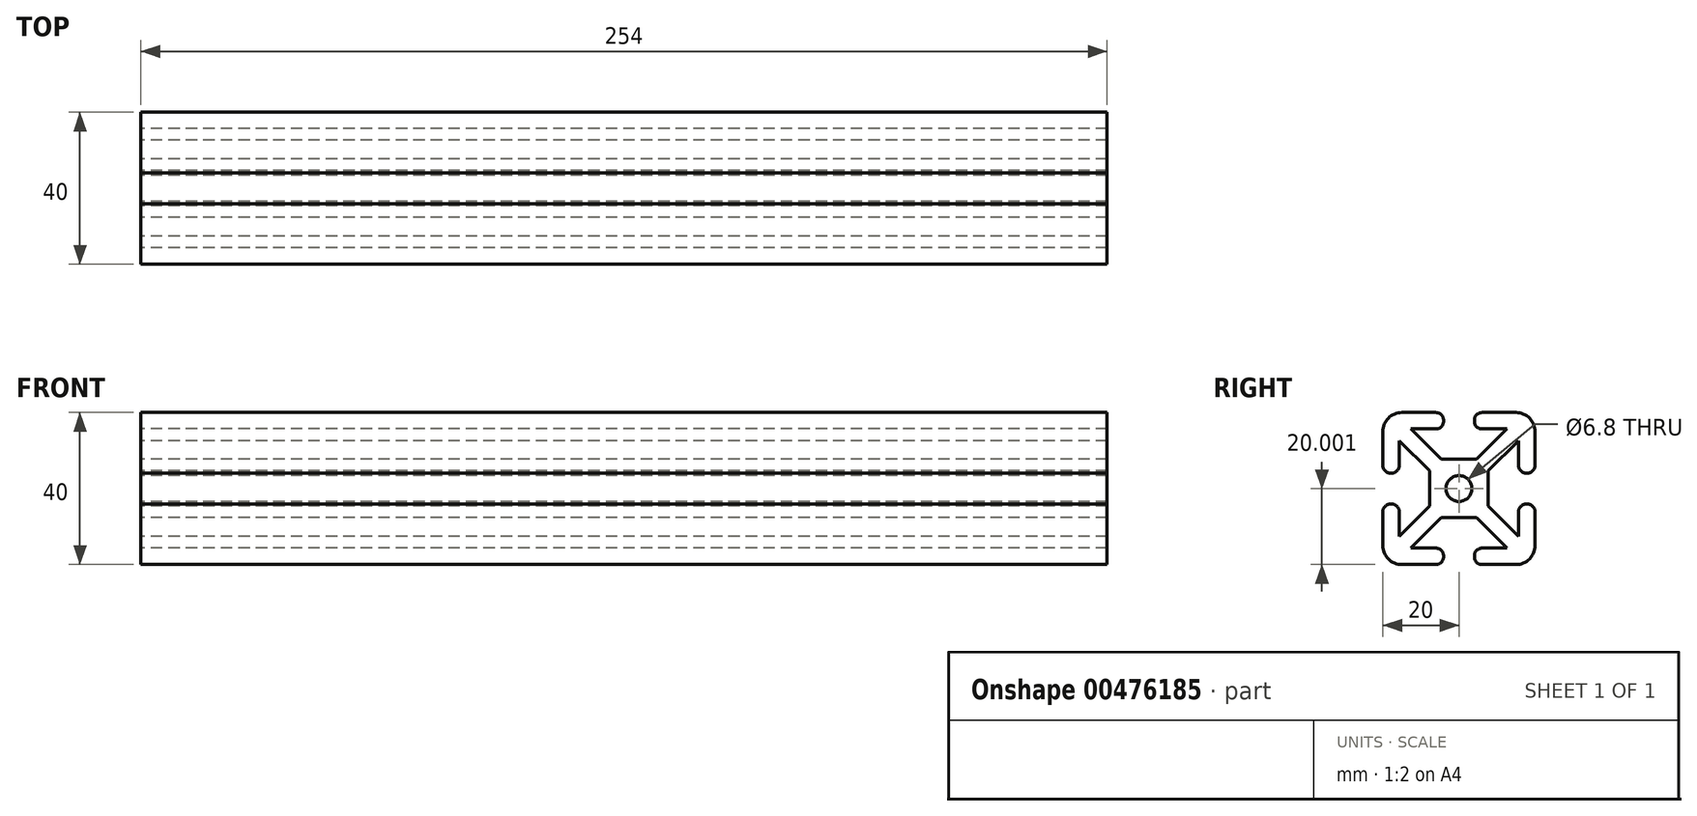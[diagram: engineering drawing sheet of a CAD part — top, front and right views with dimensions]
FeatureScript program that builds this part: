
annotation { "Feature Type Name" : "Feature", "Feature Type Description" : "" }
export const myFeature = defineFeature(function(context is Context, id is Id, definition is map)
    precondition{}
    {
        {
            var Q0;
            Q0=qCreatedBy(makeId("Right.planeOp"),FACE);
            var sketch = newSketch(context, id + "F0", { "sketchPlane" : qUnion([Q0])});
            skLineSegment(sketch, "E0", {"start": v(-15.94, 15.35) * mm, "end": v(0, 15.35) * mm});
            skLineSegment(sketch, "E1", {"start": v(0, 15.35) * mm, "end": v(8.12, 15.35) * mm, "construction": true});
            skLineSegment(sketch, "E2", {"start": v(8.12, 15.35) * mm, "end": v(24.06, 15.35) * mm});
            skLineSegment(sketch, "E3.bottom", {"start": v(-3.62, 3.04) * mm, "end": v(11.75, 3.04) * mm});
            skLineSegment(sketch, "E3.top", {"start": v(-3.62, -12.33) * mm, "end": v(11.75, -12.33) * mm});
            skLineSegment(sketch, "E3.left", {"start": v(-3.62, 3.04) * mm, "end": v(-3.62, -12.33) * mm});
            skLineSegment(sketch, "E3.right", {"start": v(11.75, 3.04) * mm, "end": v(11.75, -12.33) * mm});
            skLineSegment(sketch, "E4", {"start": v(11.74, 3.04) * mm, "end": v(24.06, 15.35) * mm, "construction": true});
            skLineSegment(sketch, "E5", {"start": v(-3.62, 3.04) * mm, "end": v(-15.94, 15.35) * mm});
            skLineSegment(sketch, "E6", {"start": v(-3.62, -12.33) * mm, "end": v(-15.94, -24.65) * mm, "construction": true});
            skLineSegment(sketch, "E7", {"start": v(11.74, -12.33) * mm, "end": v(24.06, -24.65) * mm});
            skLineSegment(sketch, "E8", {"start": v(16.5, 7.78) * mm, "end": v(14.97, 9.31) * mm, "construction": true});
            skLineSegment(sketch, "E9", {"start": v(16.5, 7.78) * mm, "end": v(18.02, 6.26) * mm, "construction": true});
            skLineSegment(sketch, "E10", {"start": v(14.97, 9.31) * mm, "end": v(21, 15.35) * mm});
            skLineSegment(sketch, "E11", {"start": v(18.02, 6.26) * mm, "end": v(24.06, 12.3) * mm});
            skLineSegment(sketch, "E12", {"start": v(14.97, 9.31) * mm, "end": v(-15.94, -21.6) * mm});
            skLineSegment(sketch, "E13", {"start": v(18.02, 6.26) * mm, "end": v(-12.89, -24.65) * mm});
            skLineSegment(sketch, "E14", {"start": v(0, 15.35) * mm, "end": v(0, 11.03) * mm});
            skLineSegment(sketch, "E15", {"start": v(8.12, 15.35) * mm, "end": v(8.12, 11.03) * mm});
            skLineSegment(sketch, "E16", {"start": v(8.12, 11.03) * mm, "end": v(16.69, 11.03) * mm});
            skLineSegment(sketch, "E17", {"start": v(0, 11.03) * mm, "end": v(-11.62, 11.03) * mm});
            skLineSegment(sketch, "E18", {"start": v(-3.62, 3.04) * mm, "end": v(11.75, -12.33) * mm});
            skLineSegment(sketch, "E19", {"start": v(11.74, 3.04) * mm, "end": v(-3.62, -12.33) * mm, "construction": true});
            skCircle(sketch, "E20", {"center": v(4.06, -4.65) * mm, "radius": 3.4 * mm});
            skLineSegment(sketch, "E21", {"start": v(24.06, -0.59) * mm, "end": v(24.06, -8.7) * mm, "construction": true});
            skLineSegment(sketch, "E22", {"start": v(24.06, -0.59) * mm, "end": v(24.06, 15.35) * mm});
            skLineSegment(sketch, "E23", {"start": v(24.06, -24.65) * mm, "end": v(24.06, -8.7) * mm});
            skLineSegment(sketch, "E24", {"start": v(24.06, -0.59) * mm, "end": v(19.74, -0.59) * mm});
            skLineSegment(sketch, "E25", {"start": v(24.06, -8.7) * mm, "end": v(19.74, -8.7) * mm});
            skLineSegment(sketch, "E26", {"start": v(19.74, -0.59) * mm, "end": v(19.74, 7.98) * mm});
            skLineSegment(sketch, "E27", {"start": v(19.74, 7.98) * mm, "end": v(16.69, 11.03) * mm});
            skLineSegment(sketch, "E28", {"start": v(-7.27, 6.68) * mm, "end": v(-8.8, 5.15) * mm});
            skLineSegment(sketch, "E29", {"start": v(-7.27, 6.68) * mm, "end": v(-5.74, 8.2) * mm});
            skLineSegment(sketch, "E30", {"start": v(-5.74, 8.2) * mm, "end": v(-12.89, 15.35) * mm});
            skLineSegment(sketch, "E31", {"start": v(-5.74, 8.2) * mm, "end": v(24.06, -21.6) * mm});
            skLineSegment(sketch, "E32", {"start": v(19.74, -8.7) * mm, "end": v(19.74, -17.27) * mm});
            skLineSegment(sketch, "E33", {"start": v(-15.94, 15.35) * mm, "end": v(-15.94, -0.59) * mm});
            skLineSegment(sketch, "E34", {"start": v(-15.94, -0.59) * mm, "end": v(-15.94, -8.7) * mm, "construction": true});
            skLineSegment(sketch, "E35", {"start": v(-15.94, -24.65) * mm, "end": v(0, -24.65) * mm});
            skLineSegment(sketch, "E36", {"start": v(0, -24.65) * mm, "end": v(8.12, -24.65) * mm, "construction": true});
            skLineSegment(sketch, "E37", {"start": v(-15.94, -8.7) * mm, "end": v(-15.94, -24.65) * mm});
            skLineSegment(sketch, "E38", {"start": v(8.12, -24.65) * mm, "end": v(24.06, -24.65) * mm});
            skLineSegment(sketch, "E39", {"start": v(-8.8, 5.15) * mm, "end": v(-15.94, 12.3) * mm});
            skLineSegment(sketch, "E40", {"start": v(-8.8, 5.15) * mm, "end": v(21, -24.65) * mm});
            skLineSegment(sketch, "E41", {"start": v(-15.94, -0.59) * mm, "end": v(-11.62, -0.59) * mm});
            skLineSegment(sketch, "E42", {"start": v(-15.94, -8.7) * mm, "end": v(-11.62, -8.7) * mm});
            skLineSegment(sketch, "E43", {"start": v(0, -24.65) * mm, "end": v(0, -20.33) * mm});
            skLineSegment(sketch, "E44", {"start": v(8.12, -24.65) * mm, "end": v(8.12, -20.33) * mm});
            skLineSegment(sketch, "E45", {"start": v(-11.62, -0.59) * mm, "end": v(-11.62, 7.98) * mm});
            skLineSegment(sketch, "E46", {"start": v(-11.62, -8.7) * mm, "end": v(-11.62, -17.27) * mm});
            skLineSegment(sketch, "E47", {"start": v(0, -20.33) * mm, "end": v(-8.57, -20.33) * mm});
            skLineSegment(sketch, "E48", {"start": v(8.12, -20.33) * mm, "end": v(16.69, -20.33) * mm});
            skSolve(sketch);
        }
        {
            var Q0;
            {var subQ0=sQuery(id+"F0.wireOp",EDGE,"E41");Q0=makeQuery(id+"F0.imprint","IMPRINT",FACE,{"disambiguationData":[TD([[makeQuery(id+"F0.imprint","IMPRINT",EDGE,{"derivedFrom":subQ0}),1.0]])]});}
            var Q1;
            {var subQ0=sQuery(id+"F0.wireOp",EDGE,"E28");Q1=makeQuery(id+"F0.imprint","IMPRINT",FACE,{"disambiguationData":[TD([[makeQuery(id+"F0.imprint","IMPRINT",EDGE,{"derivedFrom":subQ0}),-1.0]])]});}
            var Q2;
            {var subQ3=sQuery(id+"F0.wireOp",EDGE,"E29");Q2=makeQuery(id+"F0.imprint","IMPRINT",FACE,{"disambiguationData":[TD([[makeQuery(id+"F0.imprint","IMPRINT",EDGE,{"derivedFrom":subQ3}),1.0]])]});}
            var Q3;
            {var subQ0=sQuery(id+"F0.wireOp",EDGE,"E14");Q3=makeQuery(id+"F0.imprint","IMPRINT",FACE,{"disambiguationData":[TD([[makeQuery(id+"F0.imprint","IMPRINT",EDGE,{"derivedFrom":subQ0}),-1.0]])]});}
            var Q4;
            {var subQ0=sQuery(id+"F0.wireOp",EDGE,"E5");var subQ5=sQuery(id+"F0.wireOp",EDGE,"E17");var subQ6=makeQuery(id+"F0.imprint","INTERSECT",VERTEX,{"derivedFrom":[subQ0,subQ5]});Q4=makeQuery(id+"F0.imprint","IMPRINT",FACE,{"disambiguationData":[TD([[makeQuery(id+"F0.imprint","IMPRINT",EDGE,{"disambiguationData":[TD([[subQ6,1.0]])],"derivedFrom":subQ5}),-1.0]])]});}
            var Q5;
            {var subQ4=sQuery(id+"F0.wireOp",EDGE,"E42");Q5=makeQuery(id+"F0.imprint","IMPRINT",FACE,{"disambiguationData":[TD([[makeQuery(id+"F0.imprint","IMPRINT",EDGE,{"derivedFrom":subQ4}),-1.0]])]});}
            var Q6;
            {var subQ2=sQuery(id+"F0.wireOp",EDGE,"E3.left");var subQ6=sQuery(id+"F0.wireOp",EDGE,"E3.top");var subQ7=makeQuery(id+"F0.imprint","INTERSECT",VERTEX,{"derivedFrom":[subQ6,subQ2]});Q6=makeQuery(id+"F0.imprint","IMPRINT",FACE,{"disambiguationData":[TD([[makeQuery(id+"F0.imprint","IMPRINT",EDGE,{"disambiguationData":[TD([[subQ7,-1.0]])],"derivedFrom":subQ6}),-1.0]])]});}
            var Q7;
            {var subQ4=sQuery(id+"F0.wireOp",EDGE,"E43");Q7=makeQuery(id+"F0.imprint","IMPRINT",FACE,{"disambiguationData":[TD([[makeQuery(id+"F0.imprint","IMPRINT",EDGE,{"derivedFrom":subQ4}),1.0]])]});}
            var Q8;
            {var subQ3=sQuery(id+"F0.wireOp",EDGE,"E27");Q8=makeQuery(id+"F0.imprint","IMPRINT",FACE,{"disambiguationData":[TD([[makeQuery(id+"F0.imprint","IMPRINT",EDGE,{"derivedFrom":subQ3}),1.0]])]});}
            var Q9;
            {var subQ3=sQuery(id+"F0.wireOp",EDGE,"E27");Q9=makeQuery(id+"F0.imprint","IMPRINT",FACE,{"disambiguationData":[TD([[makeQuery(id+"F0.imprint","IMPRINT",EDGE,{"derivedFrom":subQ3}),-1.0]])]});}
            var Q10;
            {var subQ4=sQuery(id+"F0.wireOp",EDGE,"E24");Q10=makeQuery(id+"F0.imprint","IMPRINT",FACE,{"disambiguationData":[TD([[makeQuery(id+"F0.imprint","IMPRINT",EDGE,{"derivedFrom":subQ4}),-1.0]])]});}
            var Q11;
            {var subQ0=sQuery(id+"F0.wireOp",EDGE,"E15");Q11=makeQuery(id+"F0.imprint","IMPRINT",FACE,{"disambiguationData":[TD([[makeQuery(id+"F0.imprint","IMPRINT",EDGE,{"derivedFrom":subQ0}),1.0]])]});}
            var Q12;
            {var subQ0=sQuery(id+"F0.wireOp",EDGE,"E13");var subQ1=sQuery(id+"F0.wireOp",EDGE,"E3.right");var subQ2=makeQuery(id+"F0.imprint","INTERSECT",VERTEX,{"derivedFrom":[subQ1,subQ0]});Q12=makeQuery(id+"F0.imprint","IMPRINT",FACE,{"disambiguationData":[TD([[makeQuery(id+"F0.imprint","IMPRINT",EDGE,{"disambiguationData":[TD([[subQ2,-1.0]])],"derivedFrom":subQ1}),-1.0]])]});}
            var Q13;
            {var subQ0=sQuery(id+"F0.wireOp",EDGE,"E13");var subQ1=sQuery(id+"F0.wireOp",EDGE,"E3.top");var subQ2=makeQuery(id+"F0.imprint","INTERSECT",VERTEX,{"derivedFrom":[subQ1,subQ0]});Q13=makeQuery(id+"F0.imprint","IMPRINT",FACE,{"disambiguationData":[TD([[makeQuery(id+"F0.imprint","IMPRINT",EDGE,{"disambiguationData":[TD([[subQ2,-1.0]])],"derivedFrom":subQ1}),1.0]])]});}
            var Q14;
            {var subQ0=sQuery(id+"F0.wireOp",EDGE,"E40");var subQ1=sQuery(id+"F0.wireOp",EDGE,"E3.left");var subQ2=makeQuery(id+"F0.imprint","INTERSECT",VERTEX,{"derivedFrom":[subQ1,subQ0]});Q14=makeQuery(id+"F0.imprint","IMPRINT",FACE,{"disambiguationData":[TD([[makeQuery(id+"F0.imprint","IMPRINT",EDGE,{"disambiguationData":[TD([[subQ2,-1.0]])],"derivedFrom":subQ1}),1.0]])]});}
            var Q15;
            {var subQ0=sQuery(id+"F0.wireOp",EDGE,"E31");var subQ1=sQuery(id+"F0.wireOp",EDGE,"E3.bottom");var subQ2=makeQuery(id+"F0.imprint","INTERSECT",VERTEX,{"derivedFrom":[subQ1,subQ0]});Q15=makeQuery(id+"F0.imprint","IMPRINT",FACE,{"disambiguationData":[TD([[makeQuery(id+"F0.imprint","IMPRINT",EDGE,{"disambiguationData":[TD([[subQ2,-1.0]])],"derivedFrom":subQ1}),-1.0]])]});}
            var Q16;
            {var subQ5=sQuery(id+"F0.wireOp",EDGE,"E29");Q16=makeQuery(id+"F0.imprint","IMPRINT",FACE,{"disambiguationData":[TD([[makeQuery(id+"F0.imprint","IMPRINT",EDGE,{"derivedFrom":subQ5}),-1.0]])]});}
            var Q17;
            {var subQ5=sQuery(id+"F0.wireOp",EDGE,"E28");Q17=makeQuery(id+"F0.imprint","IMPRINT",FACE,{"disambiguationData":[TD([[makeQuery(id+"F0.imprint","IMPRINT",EDGE,{"derivedFrom":subQ5}),1.0]])]});}
            var Q18;
            {var subQ1=sQuery(id+"F0.wireOp",EDGE,"E7");Q18=makeQuery(id+"F0.imprint","IMPRINT",FACE,{"disambiguationData":[TD([[makeQuery(id+"F0.imprint","IMPRINT",EDGE,{"derivedFrom":subQ1}),-1.0]])]});}
            var Q19;
            {var subQ1=sQuery(id+"F0.wireOp",EDGE,"E7");Q19=makeQuery(id+"F0.imprint","IMPRINT",FACE,{"disambiguationData":[TD([[makeQuery(id+"F0.imprint","IMPRINT",EDGE,{"derivedFrom":subQ1}),1.0]])]});}
            var Q20;
            {var subQ0=sQuery(id+"F0.wireOp",EDGE,"E25");Q20=makeQuery(id+"F0.imprint","IMPRINT",FACE,{"disambiguationData":[TD([[makeQuery(id+"F0.imprint","IMPRINT",EDGE,{"derivedFrom":subQ0}),1.0]])]});}
            var Q21;
            {var subQ0=sQuery(id+"F0.wireOp",EDGE,"E44");Q21=makeQuery(id+"F0.imprint","IMPRINT",FACE,{"disambiguationData":[TD([[makeQuery(id+"F0.imprint","IMPRINT",EDGE,{"derivedFrom":subQ0}),-1.0]])]});}
            var Q22;
            {var subQ1=sQuery(id+"F0.wireOp",EDGE,"E3.right");var subQ6=sQuery(id+"F0.wireOp",EDGE,"E3.bottom");var subQ9=makeQuery(id+"F0.imprint","INTERSECT",VERTEX,{"derivedFrom":[subQ6,subQ1]});Q22=makeQuery(id+"F0.imprint","IMPRINT",FACE,{"disambiguationData":[TD([[makeQuery(id+"F0.imprint","IMPRINT",EDGE,{"disambiguationData":[TD([[subQ9,1.0]])],"derivedFrom":subQ6}),-1.0]])]});}
            var Q23;
            {var subQ0=sQuery(id+"F0.wireOp",EDGE,"E18");var subQ5=sQuery(id+"F0.wireOp",EDGE,"E20");var subQ6=makeQuery(id+"F0.imprint","INTERSECT",VERTEX,{"disambiguationData":[OD(0.0)],"derivedFrom":[subQ0,subQ5]});Q23=makeQuery(id+"F0.imprint","IMPRINT",FACE,{"disambiguationData":[TD([[makeQuery(id+"F0.imprint","IMPRINT",EDGE,{"disambiguationData":[TD([[subQ6,-1.0]])],"derivedFrom":subQ5}),-1.0]])]});}
            var Q24;
            {var subQ1=sQuery(id+"F0.wireOp",EDGE,"E3.top");var subQ6=sQuery(id+"F0.wireOp",EDGE,"E3.left");var subQ9=makeQuery(id+"F0.imprint","INTERSECT",VERTEX,{"derivedFrom":[subQ1,subQ6]});Q24=makeQuery(id+"F0.imprint","IMPRINT",FACE,{"disambiguationData":[TD([[makeQuery(id+"F0.imprint","IMPRINT",EDGE,{"disambiguationData":[TD([[subQ9,-1.0]])],"derivedFrom":subQ1}),1.0]])]});}
            var Q25;
            {var subQ0=sQuery(id+"F0.wireOp",EDGE,"E18");var subQ5=sQuery(id+"F0.wireOp",EDGE,"E20");var subQ6=makeQuery(id+"F0.imprint","INTERSECT",VERTEX,{"disambiguationData":[OD(1.0)],"derivedFrom":[subQ0,subQ5]});Q25=makeQuery(id+"F0.imprint","IMPRINT",FACE,{"disambiguationData":[TD([[makeQuery(id+"F0.imprint","IMPRINT",EDGE,{"disambiguationData":[TD([[subQ6,1.0]])],"derivedFrom":subQ5}),-1.0]])]});}
            var Q26;
            {var subQ0=sQuery(id+"F0.wireOp",EDGE,"E18");var subQ5=sQuery(id+"F0.wireOp",EDGE,"E20");var subQ6=makeQuery(id+"F0.imprint","INTERSECT",VERTEX,{"disambiguationData":[OD(1.0)],"derivedFrom":[subQ0,subQ5]});Q26=makeQuery(id+"F0.imprint","IMPRINT",FACE,{"disambiguationData":[TD([[makeQuery(id+"F0.imprint","IMPRINT",EDGE,{"disambiguationData":[TD([[subQ6,-1.0]])],"derivedFrom":subQ5}),-1.0]])]});}
            var Q27;
            {var subQ0=sQuery(id+"F0.wireOp",EDGE,"E18");var subQ5=sQuery(id+"F0.wireOp",EDGE,"E20");var subQ6=makeQuery(id+"F0.imprint","INTERSECT",VERTEX,{"disambiguationData":[OD(0.0)],"derivedFrom":[subQ0,subQ5]});Q27=makeQuery(id+"F0.imprint","IMPRINT",FACE,{"disambiguationData":[TD([[makeQuery(id+"F0.imprint","IMPRINT",EDGE,{"disambiguationData":[TD([[subQ6,1.0]])],"derivedFrom":subQ5}),-1.0]])]});}
            extrude(context, id + "F1", {"entities" : qUnion([Q0, Q1, Q2, Q3, Q4, Q5, Q6, Q7, Q8, Q9, Q10, Q11, Q12, Q13, Q14, Q15, Q16, Q17, Q18, Q19, Q20, Q21, Q22, Q23, Q24, Q25, Q26, Q27]), "depth" : 254 * mm});
        }
        {
            var Q0;
            Q0=makeQuery(id+"F1.opExtrude","SWEPT_EDGE",EDGE,{"disambiguationData":[OSD([sQuery(id+"F0.wireOp",EDGE,"E14"),sQuery(id+"F0.wireOp",EDGE,"E17")])]});
            var Q1;
            Q1=makeQuery(id+"F1.opExtrude","SWEPT_EDGE",EDGE,{"disambiguationData":[OSD([sQuery(id+"F0.wireOp",EDGE,"E41"),sQuery(id+"F0.wireOp",EDGE,"E45")])]});
            var Q2;
            Q2=makeQuery(id+"F1.opExtrude","SWEPT_EDGE",EDGE,{"disambiguationData":[OSD([sQuery(id+"F0.wireOp",EDGE,"E33"),sQuery(id+"F0.wireOp",EDGE,"E41")])]});
            var Q3;
            Q3=makeQuery(id+"F1.opExtrude","SWEPT_EDGE",EDGE,{"disambiguationData":[OSD([sQuery(id+"F0.wireOp",EDGE,"E0"),sQuery(id+"F0.wireOp",EDGE,"E14")])]});
            var Q4;
            Q4=makeQuery(id+"F1.opExtrude","SWEPT_EDGE",EDGE,{"disambiguationData":[OSD([sQuery(id+"F0.wireOp",EDGE,"E15"),sQuery(id+"F0.wireOp",EDGE,"E16")])]});
            var Q5;
            Q5=makeQuery(id+"F1.opExtrude","SWEPT_EDGE",EDGE,{"disambiguationData":[OSD([sQuery(id+"F0.wireOp",EDGE,"E24"),sQuery(id+"F0.wireOp",EDGE,"E26")])]});
            var Q6;
            Q6=makeQuery(id+"F1.opExtrude","SWEPT_EDGE",EDGE,{"disambiguationData":[OSD([sQuery(id+"F0.wireOp",EDGE,"E22"),sQuery(id+"F0.wireOp",EDGE,"E24")])]});
            var Q7;
            Q7=makeQuery(id+"F1.opExtrude","SWEPT_EDGE",EDGE,{"disambiguationData":[OSD([sQuery(id+"F0.wireOp",EDGE,"E38"),sQuery(id+"F0.wireOp",EDGE,"E44")])]});
            var Q8;
            Q8=makeQuery(id+"F1.opExtrude","SWEPT_EDGE",EDGE,{"disambiguationData":[OSD([sQuery(id+"F0.wireOp",EDGE,"E2"),sQuery(id+"F0.wireOp",EDGE,"E15")])]});
            var Q9;
            Q9=makeQuery(id+"F1.opExtrude","SWEPT_EDGE",EDGE,{"disambiguationData":[OSD([sQuery(id+"F0.wireOp",EDGE,"E37"),sQuery(id+"F0.wireOp",EDGE,"E42")])]});
            var Q10;
            Q10=makeQuery(id+"F1.opExtrude","SWEPT_EDGE",EDGE,{"disambiguationData":[OSD([sQuery(id+"F0.wireOp",EDGE,"E42"),sQuery(id+"F0.wireOp",EDGE,"E46")])]});
            var Q11;
            Q11=makeQuery(id+"F1.opExtrude","SWEPT_EDGE",EDGE,{"disambiguationData":[OSD([sQuery(id+"F0.wireOp",EDGE,"E35"),sQuery(id+"F0.wireOp",EDGE,"E43")])]});
            var Q12;
            Q12=makeQuery(id+"F1.opExtrude","SWEPT_EDGE",EDGE,{"disambiguationData":[OSD([sQuery(id+"F0.wireOp",EDGE,"E43"),sQuery(id+"F0.wireOp",EDGE,"E47")])]});
            var Q13;
            Q13=makeQuery(id+"F1.opExtrude","SWEPT_EDGE",EDGE,{"disambiguationData":[OSD([sQuery(id+"F0.wireOp",EDGE,"E44"),sQuery(id+"F0.wireOp",EDGE,"E48")])]});
            var Q14;
            Q14=makeQuery(id+"F1.opExtrude","SWEPT_EDGE",EDGE,{"disambiguationData":[OSD([sQuery(id+"F0.wireOp",EDGE,"E25"),sQuery(id+"F0.wireOp",EDGE,"E32")])]});
            var Q15;
            Q15=makeQuery(id+"F1.opExtrude","SWEPT_EDGE",EDGE,{"disambiguationData":[OSD([sQuery(id+"F0.wireOp",EDGE,"E23"),sQuery(id+"F0.wireOp",EDGE,"E25")])]});
            fillet(context, id + "F2", {"entities" : qUnion([Q0, Q1, Q2, Q3, Q4, Q5, Q6, Q7, Q8, Q9, Q10, Q11, Q12, Q13, Q14, Q15]), "radius" : 2 * mm, "tangentPropagation" : true, "allowEdgeOverflow" : false});
        }
        {
            var Q0;
            Q0=makeQuery(id+"F1.opExtrude","SWEPT_EDGE",EDGE,{"disambiguationData":[OSD([sQuery(id+"F0.wireOp",EDGE,"E0"),sQuery(id+"F0.wireOp",EDGE,"E5"),sQuery(id+"F0.wireOp",EDGE,"E33")])]});
            var Q1;
            Q1=makeQuery(id+"F1.opExtrude","SWEPT_EDGE",EDGE,{"disambiguationData":[OSD([sQuery(id+"F0.wireOp",EDGE,"E2"),sQuery(id+"F0.wireOp",EDGE,"E22")])]});
            var Q2;
            Q2=makeQuery(id+"F1.opExtrude","SWEPT_EDGE",EDGE,{"disambiguationData":[OSD([sQuery(id+"F0.wireOp",EDGE,"E7"),sQuery(id+"F0.wireOp",EDGE,"E23"),sQuery(id+"F0.wireOp",EDGE,"E38")])]});
            var Q3;
            Q3=makeQuery(id+"F1.opExtrude","SWEPT_EDGE",EDGE,{"disambiguationData":[OSD([sQuery(id+"F0.wireOp",EDGE,"E35"),sQuery(id+"F0.wireOp",EDGE,"E37")])]});
            fillet(context, id + "F3", {"entities" : qUnion([Q0, Q1, Q2, Q3]), "radius" : 5 * mm, "tangentPropagation" : true, "allowEdgeOverflow" : false});
        }
    });
